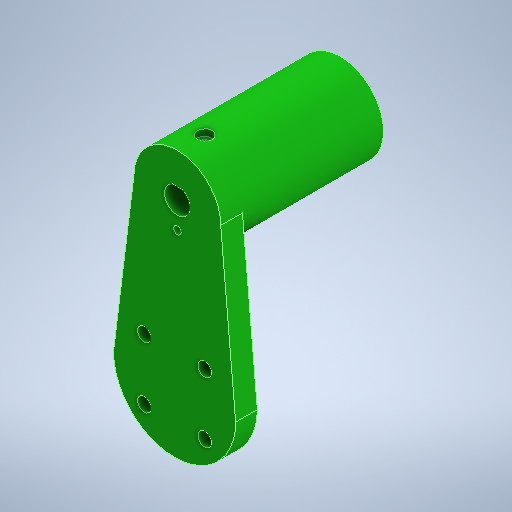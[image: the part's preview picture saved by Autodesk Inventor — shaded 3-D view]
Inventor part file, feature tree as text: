
AUTODESK INVENTOR PART (.ipt)
format: ipt  version: 2025.1 (Build 291241000, 241)  size: 318,976 bytes
history: native  units: mm
features: extrude x6, sketch x6, plane x1
ambient origin geometry x8: Origin, YZ Plane, XZ Plane, XY Plane, X Axis, Y Axis, Z Axis, Center Point
bodies: Solid1 (feature_tree)
feature tree (13):
  extrude  "Extrusion1"  Depth=5.0mm
  extrude  "Extrusion3"  Depth=32.0mm
  extrude  "Extrusion4"  Depth=9.4mm
  plane  "Work Plane2"
  extrude  "Extrusion7"  Depth=4.2869mm
  extrude  "Extrusion8"  Depth=10.0mm
  extrude  "Extrusion11"  Depth=12.0mm TaperAngle=0.0deg
  sketch  "Sketch1"  dims[d0=45.0mm d3=5.0mm]
  sketch  "Sketch5"  dims[d10=8.0mm d11=0.0mm d29=32.0mm]
  sketch  "Sketch6"  dims[d30=60.0mm d31=0.0mm d32=9.4mm]
  sketch  "Sketch9"  dims[d33=0.0mm d34=0.0mm d43=4.2869mm]
  sketch  "Sketch10"  dims[d44=32.0mm d45=10.0mm]
  sketch  "Sketch13"  dims[d46=2.7mm d47=12.0mm d48=0.0mm d49=5.5mm d50=2.5mm d51=0.0mm d52=1.5mm d57=5.0mm d58=22.274mm d59=15.821mm d60=2.8mm d61=9.562mm d62=15.0mm d63=0.0mm]
